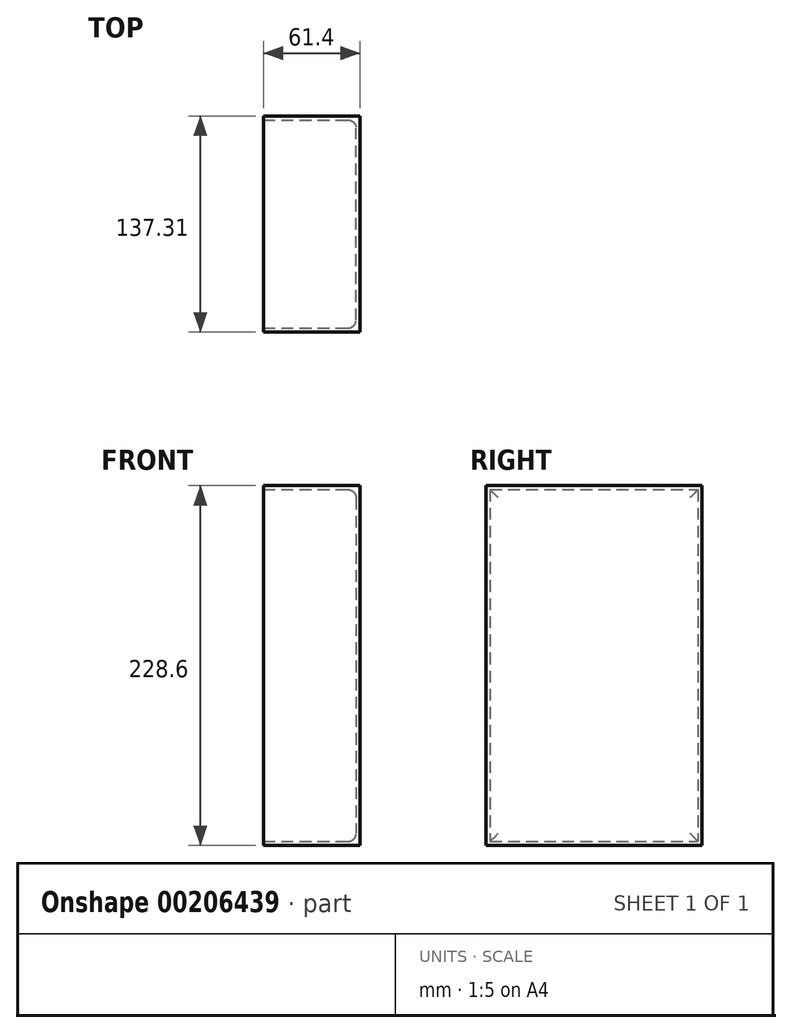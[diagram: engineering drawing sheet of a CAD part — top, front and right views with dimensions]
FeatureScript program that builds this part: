
annotation { "Feature Type Name" : "Feature", "Feature Type Description" : "" }
export const myFeature = defineFeature(function(context is Context, id is Id, definition is map)
    precondition{}
    {
        {
            var Q0;
            Q0=qCreatedBy(makeId("Top.planeOp"),FACE);
            var sketch = newSketch(context, id + "F0", { "sketchPlane" : qUnion([Q0])});
            skLineSegment(sketch, "E0.bottom", {"start": v(0, 0) * mm, "end": v(61.4, 0) * mm});
            skLineSegment(sketch, "E0.top", {"start": v(0, 137.31) * mm, "end": v(61.4, 137.31) * mm});
            skLineSegment(sketch, "E0.left", {"start": v(0, 0) * mm, "end": v(0, 137.31) * mm});
            skLineSegment(sketch, "E0.right", {"start": v(61.4, 0) * mm, "end": v(61.4, 137.31) * mm});
            skSolve(sketch);
        }
        {
            var Q0;
            Q0 = qSketchRegion(id + "F0", true);
            extrude(context, id + "F1", {"entities" : qUnion([Q0]), "depth" : 228.6 * mm});
        }
        {
            var Q0;
            Q0=makeQuery(id+"F1.opExtrude","SWEPT_FACE",FACE,{"disambiguationData":[OSD([sQuery(id+"F0.wireOp",EDGE,"E0.left")])]});
            shell(context, id + "F2", {"entities" : qUnion([Q0]), "thickness" : 2.54 * mm});
        }
        {
            var Q0;
            Q0=makeQuery(id+"F2.opShell","OFFSET_FACE",FACE,{"disambiguationData":[OSD([sQuery(id+"F0.wireOp",EDGE,"E0.right")])]});
            var sketch = newSketch(context, id + "F3", { "sketchPlane" : qUnion([Q0])});
            skLineSegment(sketch, "E1", {"start": v(-134.77, 157.06) * mm, "end": v(-2.54, 157.06) * mm});
            skLineSegment(sketch, "E2", {"start": v(-134.77, 73.37) * mm, "end": v(-2.54, 73.37) * mm});
            skSolve(sketch);
        }
        {
            var Q0;
            Q0=sQuery(id+"F3.wireOp",EDGE,"E1");
            extrude(context, id + "F4", {"bodyType" : ToolBodyType.SURFACE, "surfaceEntities" : qUnion([Q0]), "depth" : 63.5 * mm});
        }
        {
            var Q0;
            Q0=makeQuery(id+"F2.opShell","OFFSET_FACE",FACE,{"disambiguationData":[OSD([sQuery(id+"F0.wireOp",EDGE,"E0.right")])]});
            var sketch = newSketch(context, id + "F5", { "sketchPlane" : qUnion([Q0])});
            skLineSegment(sketch, "E3", {"start": v(-134.77, 81.79) * mm, "end": v(-2.54, 81.79) * mm});
            skSolve(sketch);
        }
        {
            var Q0;
            Q0=sQuery(id+"F5.wireOp",EDGE,"E3");
            extrude(context, id + "F6", {"bodyType" : ToolBodyType.SURFACE, "surfaceEntities" : qUnion([Q0]), "depth" : 58.42 * mm});
        }
        {
            var Q0;
            Q0=makeQuery(id+"F2.opShell","OFFSET_FACE",FACE,{"disambiguationData":[OSD([sQuery(id+"F0.wireOp",EDGE,"E0.right")])]});
            fillet(context, id + "F7", {"entities" : qUnion([Q0]), "radius" : 5.08 * mm, "tangentPropagation" : true, "allowEdgeOverflow" : false});
        }
    });
